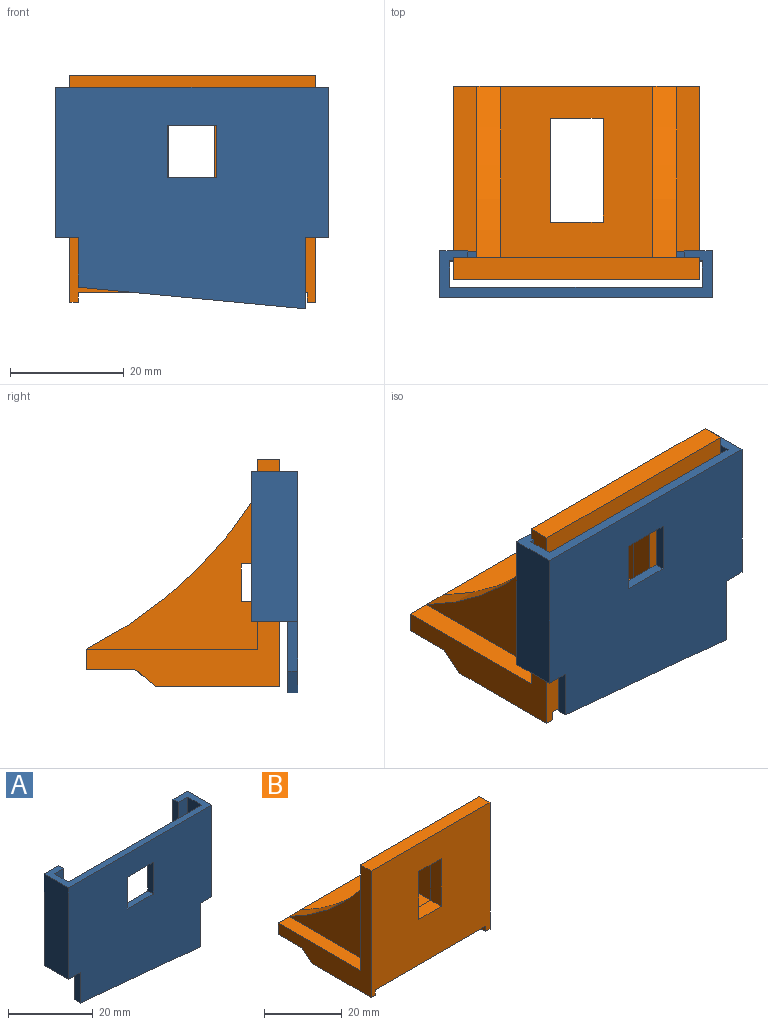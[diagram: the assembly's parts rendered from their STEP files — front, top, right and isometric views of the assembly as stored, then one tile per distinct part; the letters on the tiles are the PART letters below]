
ASSEMBLY  parts=2 mates=1
PART A: 30 faces, bbox 47.9x8.1x39 mm
  f0: plane 47.88x38.98mm, normal (0,-1,0), area 1612.6mm2, adj f7,f9,f10,f11,f12,f13,f14,f15
  f1: plane 44.4x38.98mm, normal (0,1,0), area 1520.6mm2, adj f7,f9,f10,f11,f14,f15,f16,f17
  f2: plane 26.43x7.54mm, normal (0,-1,0), area 96.1mm2, adj f4,f5,f9,f10,f17,f19,f21,f25
  f3: plane 26.43x9.28mm, normal (0,1,0), area 142mm2, adj f7,f9,f13,f18,f20,f22,f23,f24
  f4: plane 4.41x1.74mm, normal (0,0,1), area 7.7mm2, adj f2,f8,f19,f25
  f5: plane 4.41x1.74mm, normal (0,0,-1), area 7.7mm2, adj f2,f8,f21,f25
  f6: plane 26.43x7.54mm, normal (0,-1,0), area 96.1mm2, adj f7,f9,f16,f18,f20,f22,f23,f24
  f7: plane 8.13x4.88mm, normal (0,0,-1), area 23.4mm2, adj f0,f1,f3,f6,f13,f14,f16,f23
  f8: plane 26.43x9.28mm, normal (0,1,0), area 142mm2, adj f4,f5,f9,f10,f12,f19,f21,f25
  f9: plane 47.88x8.13mm, normal (0,0,1), area 116.4mm2, adj f0,f1,f2,f3,f6,f8,f12,f13
  f10: plane 8.13x4.88mm, normal (0,0,-1), area 23.4mm2, adj f0,f1,f2,f8,f12,f15,f17,f21
  f11: plane 40.01x3.8mm, normal (-0.09,0,-1), area 69.9mm2, adj f0,f1,f14,f15
  f12: plane 26.43x8.13mm, normal (-1,0,0), area 214.8mm2, adj f0,f8,f9,f10
  f13: plane 26.43x8.13mm, normal (1,0,0), area 214.8mm2, adj f0,f3,f7,f9
  f14: plane 12.55x1.74mm, normal (1,0,0), area 21.8mm2, adj f0,f1,f7,f11
  f15: plane 8.76x1.74mm, normal (-1,0,0), area 15.2mm2, adj f0,f1,f10,f11
  f16: plane 26.43x4.65mm, normal (-1,0,0), area 122.8mm2, adj f1,f6,f7,f9
  f17: plane 26.43x4.65mm, normal (1,0,0), area 122.8mm2, adj f1,f2,f9,f10
  f18: plane 4.41x1.74mm, normal (0,0,1), area 7.7mm2, adj f3,f6,f20,f24
  f19: plane 15.56x1.74mm, normal (1,0,0), area 27.1mm2, adj f2,f4,f8,f9
  f20: plane 15.56x1.74mm, normal (-1,0,0), area 27.1mm2, adj f3,f6,f9,f18
  f21: plane 7.89x1.74mm, normal (1,0,0), area 13.7mm2, adj f2,f5,f8,f10
  f22: plane 4.41x1.74mm, normal (0,0,-1), area 7.7mm2, adj f3,f6,f23,f24
  f23: plane 7.89x1.74mm, normal (-1,0,0), area 13.7mm2, adj f3,f6,f7,f22
  f24: plane 2.98x1.74mm, normal (-1,0,0), area 5.2mm2, adj f3,f6,f18,f22
  f25: plane 2.98x1.74mm, normal (1,0,0), area 5.2mm2, adj f2,f4,f5,f8
  f26: plane 8.64x1.74mm, normal (0,0,1), area 15mm2, adj f0,f1,f27,f29
  f27: plane 9.16x1.74mm, normal (1,0,0), area 15.9mm2, adj f0,f1,f26,f28
  f28: plane 8.64x1.74mm, normal (0,0,-1), area 15mm2, adj f0,f1,f27,f29
  f29: plane 9.16x1.74mm, normal (-1,0,0), area 15.9mm2, adj f0,f1,f26,f28
PART B: 37 faces, bbox 43.3x34x39.9 mm
  f0: plane 39.93x34.01mm, normal (1,0,0), area 321.7mm2, adj f4,f10,f18,f19,f20,f21,f34,f36
  f1: plane 18.26x4.88mm, normal (1,0,0), area 84.2mm2, adj f2,f8,f11,f16,f34,f35
  f2: plane 9.27x3.57mm, normal (0,-1,0), area 33.1mm2, adj f1,f3,f16,f34
  f3: plane 18.26x4.88mm, normal (-1,0,0), area 84.2mm2, adj f2,f8,f11,f16,f34,f36
  f4: plane 43.26x3.57mm, normal (0,1,0), area 154.4mm2, adj f0,f5,f16,f17,f20,f32,f33,f34
  f5: plane 39.93x34.01mm, normal (-1,0,0), area 321.7mm2, adj f4,f9,f10,f17,f18,f21,f34,f35
  f6: plane 23.89x1.68mm, normal (-1,0,0), area 38.3mm2, adj f8,f10,f19,f36
  f7: plane 23.89x1.68mm, normal (1,0,0), area 38.3mm2, adj f8,f9,f10,f35
  f8: plane 40.21x23.89mm, normal (0,0,-1), area 833.3mm2, adj f1,f3,f6,f7,f10,f11,f35,f36
  f9: plane 21.86x1.52mm, normal (0,0,-1), area 33.3mm2, adj f5,f7,f10,f35
  f10: plane 43.26x39.93mm, normal (0,-1,0), area 1535.5mm2, adj f0,f5,f6,f7,f8,f9,f19,f21
  f11: plane 9.27x4.88mm, normal (0,1,0), area 45.2mm2, adj f1,f3,f8,f16
  f12: plane 30.12x27.29mm, normal (-1,0,0), area 317mm2, adj f17,f18,f29,f30,f31,f33
  f13: plane 30.12x27.29mm, normal (1,0,0), area 317mm2, adj f16,f18,f29,f30,f31,f33
  f14: plane 30.12x27.29mm, normal (-1,0,0), area 317mm2, adj f16,f18,f26,f27,f28,f32
  f15: plane 30.12x27.29mm, normal (1,0,0), area 317mm2, adj f18,f20,f26,f27,f28,f32
  f16: plane 30.12x26.75mm, normal (0,0,1), area 636.4mm2, adj f1,f2,f3,f4,f11,f13,f14,f18
  f17: plane 30.12x4.06mm, normal (0,0,1), area 122.4mm2, adj f4,f5,f12,f18
  f18: plane 43.26x33.38mm, normal (0,1,0), area 1146mm2, adj f0,f5,f12,f13,f14,f15,f16,f17
  f19: plane 21.86x1.52mm, normal (0,0,-1), area 33.3mm2, adj f0,f6,f10,f36
  f20: plane 30.12x4.06mm, normal (0,0,1), area 122.4mm2, adj f0,f4,f15,f18
  f21: plane 43.26x3.89mm, normal (0,0,1), area 168.1mm2, adj f0,f5,f10,f18
  f22: plane 8.22x3.89mm, normal (0,0,-1), area 32mm2, adj f10,f18,f23,f25
  f23: plane 15.11x3.89mm, normal (1,0,0), area 58.7mm2, adj f10,f18,f22,f24
  f24: plane 8.22x3.89mm, normal (0,0,1), area 32mm2, adj f10,f18,f23,f25
  f25: plane 15.11x3.89mm, normal (-1,0,0), area 58.7mm2, adj f10,f18,f22,f24
  f26: plane 6.6x4.19mm, normal (0,-1,0), area 27.7mm2, adj f14,f15,f27,f28
  f27: plane 4.19x2.87mm, normal (0,0,-1), area 12mm2, adj f14,f15,f18,f26
  f28: plane 4.19x2.87mm, normal (0,0,1), area 12mm2, adj f14,f15,f18,f26
  f29: plane 4.19x2.87mm, normal (0,0,1), area 12mm2, adj f12,f13,f18,f31
  f30: plane 4.19x2.87mm, normal (0,0,-1), area 12mm2, adj f12,f13,f18,f31
  f31: plane 6.6x4.19mm, normal (0,-1,0), area 27.7mm2, adj f12,f13,f29,f30
  f32: cylinder r=76.2mm len=30.12mm, axis (-1,0,0), area 172.4mm2, adj f4,f14,f15,f18
  f33: cylinder r=76.2mm len=30.12mm, axis (-1,0,0), area 172.4mm2, adj f4,f12,f13,f18
  f34: plane 43.26x8.53mm, normal (0,0,-1), area 341.8mm2, adj f0,f1,f2,f3,f4,f5,f35,f36
  f35: plane 16.99x3.62mm, normal (0,0.64,-0.77), area 39mm2, adj f1,f5,f7,f8,f9,f34
  f36: plane 16.99x3.62mm, normal (0,0.64,-0.77), area 39mm2, adj f0,f3,f6,f8,f19,f34
PLACE A t=(-30.03,-21.86,-18.97)mm
PLACE B t=(-51.52,-26.88,-37.13)mm
MATE parallel B.f10 <-> A.f1  axis (0,-1,0) through (-29.87,-26.88,-16.62)mm
